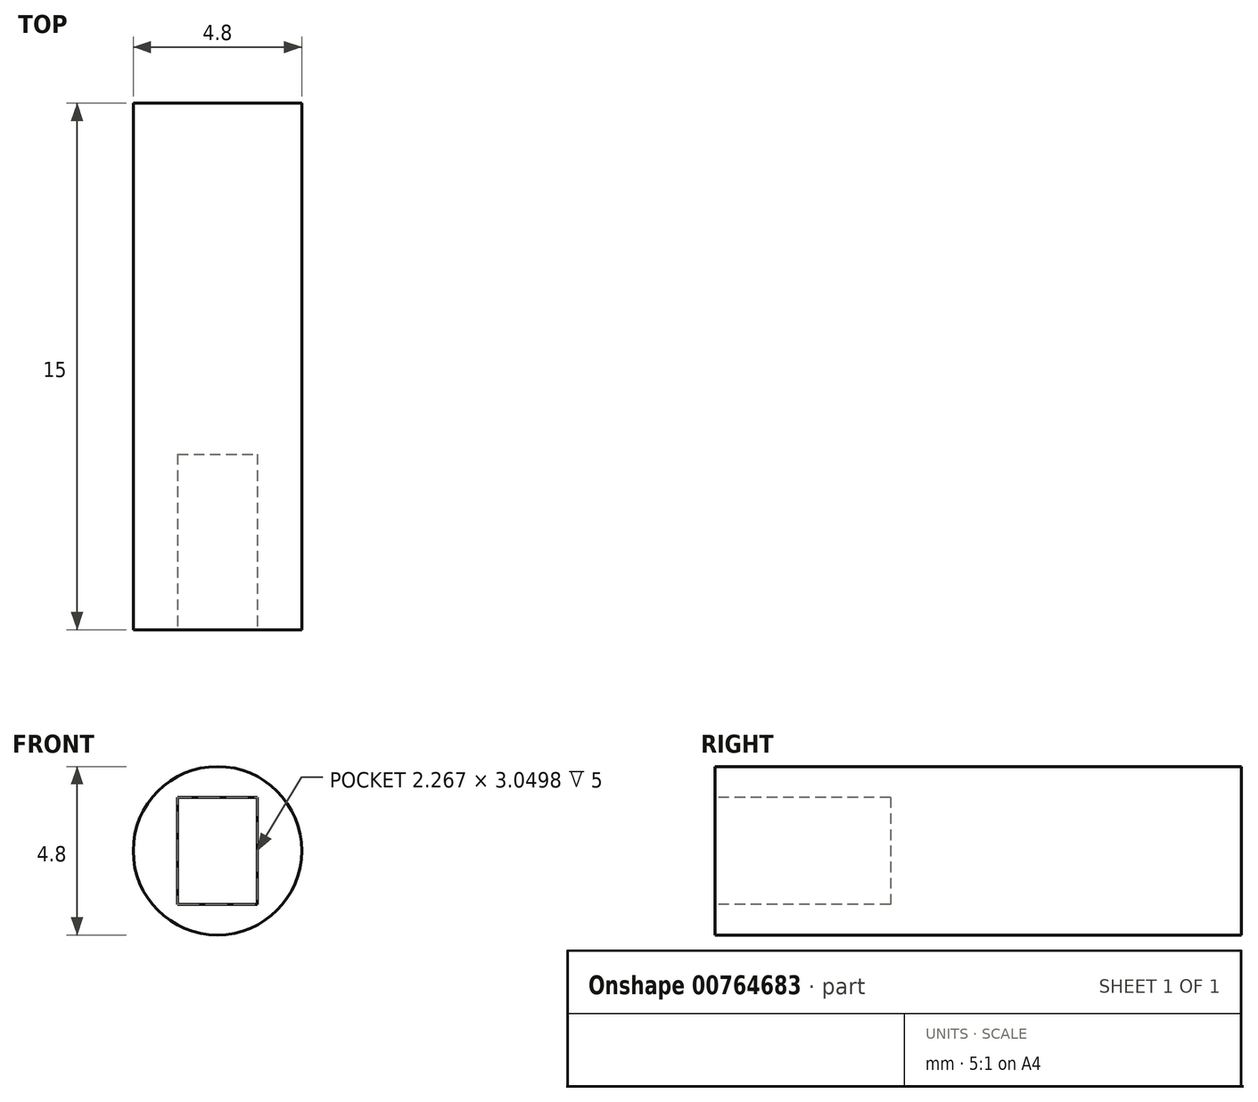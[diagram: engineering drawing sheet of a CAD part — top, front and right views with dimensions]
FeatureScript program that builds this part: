
annotation { "Feature Type Name" : "Feature", "Feature Type Description" : "" }
export const myFeature = defineFeature(function(context is Context, id is Id, definition is map)
    precondition{}
    {
        {
            var Q0;
            Q0=qCreatedBy(makeId("Front.planeOp"),FACE);
            var sketch = newSketch(context, id + "F0", { "sketchPlane" : qUnion([Q0])});
            skCircle(sketch, "E0", {"center": v(0, 0) * mm, "radius": 2.4 * mm});
            skSolve(sketch);
        }
        {
            var Q0;
            Q0=makeQuery(id+"F0.imprint","IMPRINT",FACE,{"disambiguationData":[TD([[makeQuery(id+"F0.imprint","IMPRINT",EDGE,{"derivedFrom":sQuery(id+"F0.wireOp",EDGE,"E0")}),1.0]])]});
            extrude(context, id + "F1", {"entities" : qUnion([Q0]), "depth" : 15 * mm, "offsetDistance" : 25 * mm});
        }
        {
            var Q0;
            Q0=makeQuery(id+"F1.opExtrude","CAP_FACE",FACE,{"disambiguationData":[OSD([sQuery(id+"F0.wireOp",EDGE,"E0")])],"isStart":false});
            var sketch = newSketch(context, id + "F2", { "sketchPlane" : qUnion([Q0])});
            skLineSegment(sketch, "E1.bottom", {"start": v(-1.13, 1.52) * mm, "end": v(1.13, 1.52) * mm});
            skLineSegment(sketch, "E1.top", {"start": v(-1.13, -1.52) * mm, "end": v(1.13, -1.52) * mm});
            skLineSegment(sketch, "E1.left", {"start": v(-1.13, 1.52) * mm, "end": v(-1.13, -1.52) * mm});
            skLineSegment(sketch, "E1.right", {"start": v(1.13, 1.52) * mm, "end": v(1.13, -1.52) * mm});
            skSolve(sketch);
        }
        {
            var Q0;
            Q0 = qSketchRegion(id + "F2", true);
            extrude(context, id + "F3", {"entities" : qUnion([Q0]), "operationType" : NewBodyOperationType.REMOVE, "oppositeDirection" : true, "depth" : 5 * mm, "offsetDistance" : 25 * mm});
        }
    });
